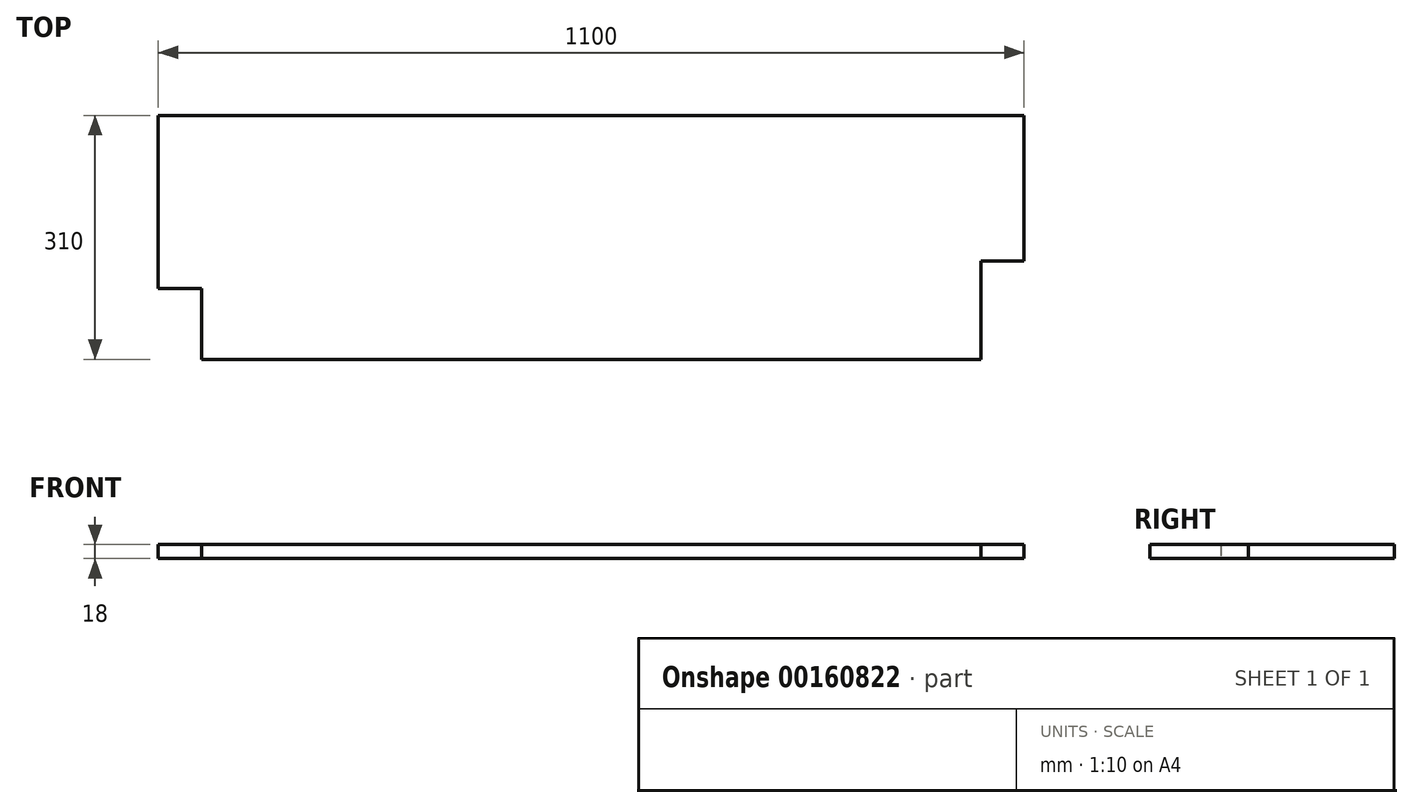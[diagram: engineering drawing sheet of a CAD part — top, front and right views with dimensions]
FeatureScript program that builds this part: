
annotation { "Feature Type Name" : "Feature", "Feature Type Description" : "" }
export const myFeature = defineFeature(function(context is Context, id is Id, definition is map)
    precondition{}
    {
        {
            var Q0;
            Q0=qCreatedBy(makeId("Top.planeOp"),FACE);
            var sketch = newSketch(context, id + "F0", { "sketchPlane" : qUnion([Q0])});
            skLineSegment(sketch, "E0.bottom", {"start": v(-1.2, 0.1) * mm, "end": v(1098.8, 0.1) * mm});
            skLineSegment(sketch, "E0.top", {"start": v(53.8, -309.9) * mm, "end": v(1043.8, -309.9) * mm});
            skLineSegment(sketch, "E0.left", {"start": v(-1.2, 0.1) * mm, "end": v(-1.2, -219.9) * mm});
            skLineSegment(sketch, "E0.right", {"start": v(1098.8, 0.1) * mm, "end": v(1098.8, -184.9) * mm});
            skLineSegment(sketch, "E1.top", {"start": v(1098.8, -184.9) * mm, "end": v(1043.8, -184.9) * mm});
            skLineSegment(sketch, "E1.right", {"start": v(1043.8, -309.9) * mm, "end": v(1043.8, -184.9) * mm});
            skLineSegment(sketch, "E2.top", {"start": v(-1.2, -219.9) * mm, "end": v(53.8, -219.9) * mm});
            skLineSegment(sketch, "E2.right", {"start": v(53.8, -309.9) * mm, "end": v(53.8, -219.9) * mm});
            skSolve(sketch);
        }
        {
            var Q0;
            Q0=makeQuery(id+"F0.imprint","IMPRINT",FACE,{"disambiguationData":[TD([[makeQuery(id+"F0.imprint","IMPRINT",EDGE,{"derivedFrom":sQuery(id+"F0.wireOp",EDGE,"E0.bottom")}),-1.0]])]});
            extrude(context, id + "F1", {"entities" : qUnion([Q0]), "depth" : 18 * mm});
        }
    });
